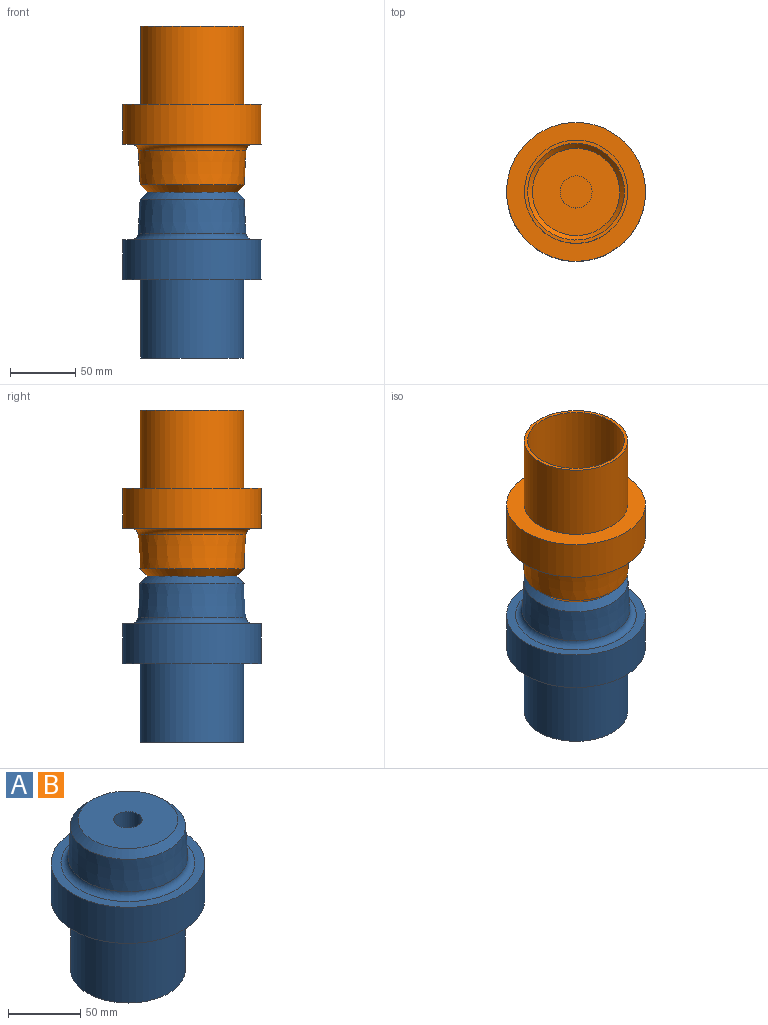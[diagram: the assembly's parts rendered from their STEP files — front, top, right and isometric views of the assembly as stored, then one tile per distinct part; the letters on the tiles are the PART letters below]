
ASSEMBLY  parts=2 mates=1
PART A: 21 faces, bbox 111.8x111.8x127 mm
  f0: cone r=39.52mm half-angle=3deg, axis (0,0,-1), area 6703.8mm2, adj f7,f8
  f1: plane 68.89x68.89mm, normal (0,0,1), area 3429.2mm2, adj f8,f9
  f2: cylinder r=53.14mm len=106.29mm, axis (0,0,-1), area 10190mm2, adj f3,f4
  f3: plane 106.29x106.29mm, normal (0,0,1), area 2150.3mm2, adj f2,f7
  f4: plane 106.29x106.29mm, normal (0,0,-1), area 3964.7mm2, adj f2,f6
  f5: plane 79.05x79.05mm, normal (0,0,-1), area 610.5mm2, adj f6,f16
  f6: cylinder r=39.52mm len=79.05mm, axis (0,0,-1), area 14899mm2, adj f4,f5
  f7: torus R=46.26mm, axis (0,0,1), area 2088.2mm2, adj f0,f3
  f8: cone r=34.44mm half-angle=45deg, axis (0,0,-1), area 1768.5mm2, adj f0,f1
  f9: cylinder r=9.74mm len=25.4mm, axis (0,0,1), area 1554.1mm2, adj f1,f10
  f10: plane 19.48x19.48mm, normal (0,0,1), area 297.9mm2, adj f9
  f11: cone r=36.99mm half-angle=3deg, axis (0,0,-1), area 6055.4mm2, adj f17,f18
  f12: plane 66.78x66.78mm, normal (0,0,-1), area 3029.3mm2, adj f18,f19
  f13: cylinder r=50.6mm len=101.21mm, axis (0,0,-1), area 8087.8mm2, adj f14,f15
  f14: plane 101.21x101.21mm, normal (0,0,-1), area 1322.4mm2, adj f13,f17
  f15: plane 101.21x101.21mm, normal (0,0,1), area 3747.4mm2, adj f13,f16
  f16: cylinder r=36.98mm len=73.97mm, axis (0,0,-1), area 14531.8mm2, adj f5,f15
  f17: torus R=46.26mm, axis (0,0,1), area 3017.1mm2, adj f11,f14
  f18: cone r=32.65mm half-angle=45deg, axis (0,0,-1), area 1233.9mm2, adj f11,f12
  f19: cylinder r=12.28mm len=25.4mm, axis (0,0,1), area 1959.5mm2, adj f12,f20
  f20: plane 24.56x24.56mm, normal (0,0,-1), area 473.6mm2, adj f19
PART B: same geometry as A
PLACE A t=(41.9,56.96,-14.34)mm
PLACE B rot(axis=(1,0,0),180deg) t=(41.9,56.96,239.66)mm
MATE parallel B.f0 <-> A.f0  axis (0,0,-1) through (41.9,56.96,112.66)mm
